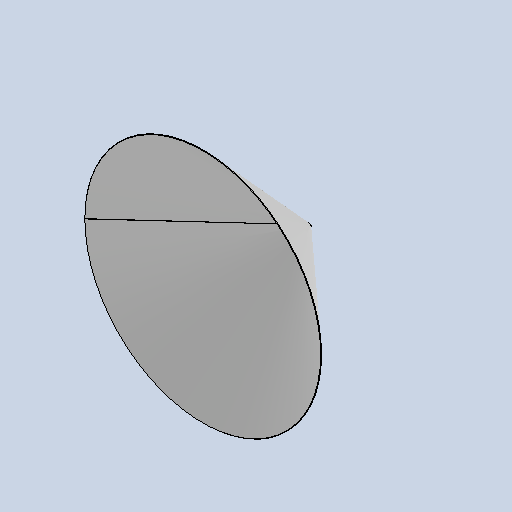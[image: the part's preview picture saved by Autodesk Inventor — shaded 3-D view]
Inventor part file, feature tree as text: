
AUTODESK INVENTOR PART (.ipt)
format: ipt  version: 2025 (Build 290162010, 162A)  size: 132,608 bytes
history: native  units: mm
features: other x2, revolve x1, sketch x1
ambient origin geometry x8: Origin, YZ Plane, XZ Plane, XY Plane, X Axis, Y Axis, Z Axis, Center Point
bodies: Solid1 (feature_tree)
feature tree (4):
  revolve  "Revolution1"  [1 undecoded]
  other  "A-Side Definition"
  sketch  "Sketch1"  dims[d0=0.8mm d3=300.0mm d4=135.0mm d5=5.0mm d6=62.8144mm]
  other  "Definition1"
note: 1 required parameter value undecoded (feature->parameter linkage not recoverable at this tier; creation-order binding heuristic only, values carry confidence <= 0.55)
